# Revit family: 201_ROL __45-1
name_source: partatom
category: Air Terminals
units: mm (PartAtom-declared; Revit-internal decimal feet)

## family parameters
Always vertical = Yes
Cut with Voids When Loaded = No
Part Type = Normal
Room Calculation Point = Yes
Round Connector Dimension = Use Diameter
Shared = No
Work Plane-Based = No

## types (7) — shared parameters
CAT0 = Yes
CL_Location_5000 = 5000 mm  [stored 16.4042 ft]
Description = Supply air duct, length 1500mm
L23 = 754 mm  [stored 2.47375 ft]
L4 = 1508 mm  [stored 4.94751 ft]
L_ARR = 400 mm  [stored 1.31234 ft]
Manufacturer = Climecon
QmdConnectorList = 201;D
URL = www.climecon.fi
W_ARR = 400 mm  [stored 1.31234 ft]
XRefLineVPlnId = 7453
YRefLineVPlnId = 7456
magiPartTypeId = 201
magiProductFamilyId = ROL */45-1
zero-valued in all types: CLBTZ, H_ARR, MC_Default_elevation

## per-type parameters (varying)
| type | D | D1 | D12 |
| ROL 125/45-1 | 125 mm | 130 mm  [stored 0.426509 ft] | 65 mm  [stored 0.213255 ft] |
| ROL 500/45-1 | 500 mm | 505 mm  [stored 1.65682 ft] | 253 mm |
| ROL 400/45-1 | 400 mm | 405 mm  [stored 1.32874 ft] | 203 mm |
| ROL 315/45-1 | 315 mm | 320 mm  [stored 1.04987 ft] | 160 mm  [stored 0.524934 ft] |
| ROL 250/45-1 | 250 mm | 255 mm  [stored 0.836614 ft] | 128 mm |
| ROL 200/45-1 | 200 mm | 205 mm  [stored 0.672572 ft] | 103 mm |
| ROL 160/45-1 | 160 mm | 165 mm  [stored 0.541339 ft] | 83 mm |

note: column(s) folded — value = type name in every type: magiProductCode, magiProductId

note: [stored X ft] marks values corroborated as IEEE doubles in the binary element streams (Revit-internal decimal feet)

## geometry (parser evidence)
native form markers: Sweep x2
no freeform markers — native parametric forms only
